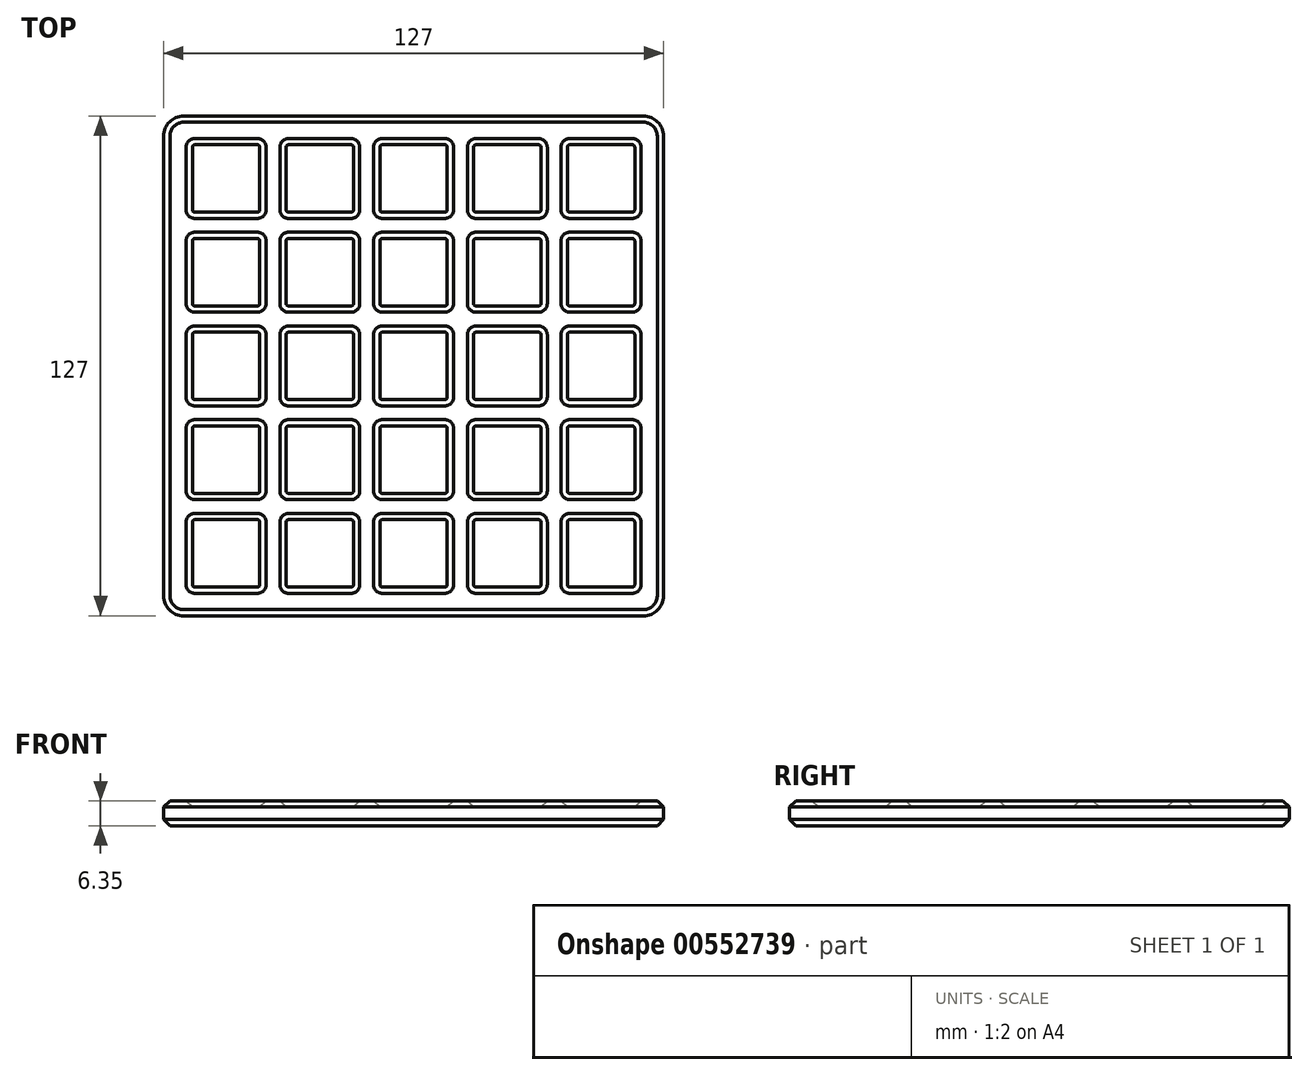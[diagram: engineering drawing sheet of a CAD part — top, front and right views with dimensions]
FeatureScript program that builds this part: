
annotation { "Feature Type Name" : "Feature", "Feature Type Description" : "" }
export const myFeature = defineFeature(function(context is Context, id is Id, definition is map)
    precondition{}
    {
        {
            var Q0;
            Q0=qCreatedBy(makeId("Top.planeOp"),FACE);
            var sketch = newSketch(context, id + "F0", { "sketchPlane" : qUnion([Q0])});
            skLineSegment(sketch, "E0.bottom", {"start": v(63.5, 63.5) * mm, "end": v(-63.5, 63.5) * mm});
            skLineSegment(sketch, "E0.top", {"start": v(63.5, -63.5) * mm, "end": v(-63.5, -63.5) * mm});
            skLineSegment(sketch, "E0.left", {"start": v(63.5, 63.5) * mm, "end": v(63.5, -63.5) * mm});
            skLineSegment(sketch, "E0.right", {"start": v(-63.5, 63.5) * mm, "end": v(-63.5, -63.5) * mm});
            skPoint(sketch, "E0.middle", {"position": v(0, 0) * mm});
            skLineSegment(sketch, "E1.bottom", {"start": v(8.57, 8.57) * mm, "end": v(-8.57, 8.57) * mm});
            skLineSegment(sketch, "E1.top", {"start": v(8.57, -8.57) * mm, "end": v(-8.57, -8.57) * mm});
            skLineSegment(sketch, "E1.left", {"start": v(8.57, 8.57) * mm, "end": v(8.57, -8.57) * mm});
            skLineSegment(sketch, "E1.right", {"start": v(-8.57, 8.57) * mm, "end": v(-8.57, -8.57) * mm});
            skLineSegment(sketch, "E2.1.0.0", {"start": v(32.39, 8.57) * mm, "end": v(15.24, 8.57) * mm});
            skLineSegment(sketch, "E2.1.0.1", {"start": v(15.24, 8.57) * mm, "end": v(15.24, -8.57) * mm});
            skLineSegment(sketch, "E2.1.0.2", {"start": v(32.39, -8.57) * mm, "end": v(15.24, -8.57) * mm});
            skLineSegment(sketch, "E2.1.0.3", {"start": v(32.39, 8.57) * mm, "end": v(32.39, -8.57) * mm});
            skLineSegment(sketch, "E2.2.0.0", {"start": v(56.2, 8.57) * mm, "end": v(39.05, 8.57) * mm});
            skLineSegment(sketch, "E2.2.0.1", {"start": v(39.05, 8.57) * mm, "end": v(39.05, -8.57) * mm});
            skLineSegment(sketch, "E2.2.0.2", {"start": v(56.2, -8.57) * mm, "end": v(39.05, -8.57) * mm});
            skLineSegment(sketch, "E2.2.0.3", {"start": v(56.2, 8.57) * mm, "end": v(56.2, -8.57) * mm});
            skLineSegment(sketch, "E2.direction1", {"start": v(-8.57, 8.57) * mm, "end": v(15.24, 8.57) * mm, "construction": true});
            skLineSegment(sketch, "E2.direction2", {"start": v(-8.57, 8.57) * mm, "end": v(-8.57, 32.39) * mm, "construction": true});
            skLineSegment(sketch, "E3.0.0.1", {"start": v(8.57, 32.39) * mm, "end": v(-8.57, 32.39) * mm});
            skLineSegment(sketch, "E3.3.0.1", {"start": v(-8.57, 32.39) * mm, "end": v(-8.57, 15.24) * mm});
            skLineSegment(sketch, "E3.6.0.1", {"start": v(8.57, 15.24) * mm, "end": v(-8.57, 15.24) * mm});
            skLineSegment(sketch, "E3.9.0.1", {"start": v(8.57, 32.39) * mm, "end": v(8.57, 15.24) * mm});
            skLineSegment(sketch, "E3.0.0.2", {"start": v(8.57, 56.2) * mm, "end": v(-8.57, 56.2) * mm});
            skLineSegment(sketch, "E3.3.0.2", {"start": v(-8.57, 56.2) * mm, "end": v(-8.57, 39.05) * mm});
            skLineSegment(sketch, "E3.6.0.2", {"start": v(8.57, 39.05) * mm, "end": v(-8.57, 39.05) * mm});
            skLineSegment(sketch, "E3.9.0.2", {"start": v(8.57, 56.2) * mm, "end": v(8.57, 39.05) * mm});
            skLineSegment(sketch, "E3.0.1.1", {"start": v(32.39, 32.39) * mm, "end": v(15.24, 32.39) * mm});
            skLineSegment(sketch, "E3.3.1.1", {"start": v(15.24, 32.39) * mm, "end": v(15.24, 15.24) * mm});
            skLineSegment(sketch, "E3.6.1.1", {"start": v(32.39, 15.24) * mm, "end": v(15.24, 15.24) * mm});
            skLineSegment(sketch, "E3.9.1.1", {"start": v(32.39, 32.39) * mm, "end": v(32.39, 15.24) * mm});
            skLineSegment(sketch, "E3.0.1.2", {"start": v(32.38, 56.2) * mm, "end": v(15.24, 56.2) * mm});
            skLineSegment(sketch, "E3.3.1.2", {"start": v(15.24, 56.2) * mm, "end": v(15.24, 39.05) * mm});
            skLineSegment(sketch, "E3.6.1.2", {"start": v(32.38, 39.05) * mm, "end": v(15.24, 39.05) * mm});
            skLineSegment(sketch, "E3.9.1.2", {"start": v(32.38, 56.2) * mm, "end": v(32.38, 39.05) * mm});
            skLineSegment(sketch, "E3.0.2.1", {"start": v(56.2, 32.39) * mm, "end": v(39.05, 32.39) * mm});
            skLineSegment(sketch, "E3.3.2.1", {"start": v(39.05, 32.39) * mm, "end": v(39.05, 15.24) * mm});
            skLineSegment(sketch, "E3.6.2.1", {"start": v(56.2, 15.24) * mm, "end": v(39.05, 15.24) * mm});
            skLineSegment(sketch, "E3.9.2.1", {"start": v(56.2, 32.39) * mm, "end": v(56.2, 15.24) * mm});
            skLineSegment(sketch, "E3.0.2.2", {"start": v(56.2, 56.2) * mm, "end": v(39.05, 56.2) * mm});
            skLineSegment(sketch, "E3.3.2.2", {"start": v(39.05, 56.2) * mm, "end": v(39.05, 39.05) * mm});
            skLineSegment(sketch, "E3.6.2.2", {"start": v(56.2, 39.05) * mm, "end": v(39.05, 39.05) * mm});
            skLineSegment(sketch, "E3.9.2.2", {"start": v(56.2, 56.2) * mm, "end": v(56.2, 39.05) * mm});
            skLineSegment(sketch, "E4.1.0.0", {"start": v(-32.39, 8.57) * mm, "end": v(-32.39, 32.39) * mm, "construction": true});
            skLineSegment(sketch, "E4.1.0.1", {"start": v(-32.39, 8.57) * mm, "end": v(-32.39, -8.57) * mm});
            skLineSegment(sketch, "E4.1.0.2", {"start": v(-15.24, 8.57) * mm, "end": v(-15.24, -8.57) * mm});
            skLineSegment(sketch, "E4.1.0.3", {"start": v(-15.24, 32.39) * mm, "end": v(-32.39, 32.39) * mm});
            skLineSegment(sketch, "E4.1.0.4", {"start": v(-15.24, 56.2) * mm, "end": v(-32.39, 56.2) * mm});
            skLineSegment(sketch, "E4.1.0.5", {"start": v(-15.24, 56.2) * mm, "end": v(-15.24, 39.05) * mm});
            skLineSegment(sketch, "E4.1.0.6", {"start": v(-15.24, -8.57) * mm, "end": v(-32.39, -8.57) * mm});
            skLineSegment(sketch, "E4.1.0.7", {"start": v(-15.24, 8.57) * mm, "end": v(-32.39, 8.57) * mm});
            skLineSegment(sketch, "E4.1.0.9", {"start": v(-32.39, 56.2) * mm, "end": v(-32.39, 39.05) * mm});
            skLineSegment(sketch, "E4.1.0.10", {"start": v(-15.24, 15.24) * mm, "end": v(-32.39, 15.24) * mm});
            skLineSegment(sketch, "E4.1.0.11", {"start": v(-15.24, 39.05) * mm, "end": v(-32.39, 39.05) * mm});
            skLineSegment(sketch, "E4.1.0.12", {"start": v(-15.24, 32.39) * mm, "end": v(-15.24, 15.24) * mm});
            skLineSegment(sketch, "E4.1.0.14", {"start": v(-32.39, 32.39) * mm, "end": v(-32.39, 15.24) * mm});
            skLineSegment(sketch, "E4.2.0.0", {"start": v(-56.2, 8.57) * mm, "end": v(-56.2, 32.38) * mm, "construction": true});
            skLineSegment(sketch, "E4.2.0.1", {"start": v(-56.2, 8.57) * mm, "end": v(-56.2, -8.57) * mm});
            skLineSegment(sketch, "E4.2.0.2", {"start": v(-39.05, 8.57) * mm, "end": v(-39.05, -8.57) * mm});
            skLineSegment(sketch, "E4.2.0.3", {"start": v(-39.05, 32.39) * mm, "end": v(-56.2, 32.39) * mm});
            skLineSegment(sketch, "E4.2.0.4", {"start": v(-39.05, 56.2) * mm, "end": v(-56.2, 56.2) * mm});
            skLineSegment(sketch, "E4.2.0.5", {"start": v(-39.05, 56.2) * mm, "end": v(-39.05, 39.05) * mm});
            skLineSegment(sketch, "E4.2.0.6", {"start": v(-39.05, -8.57) * mm, "end": v(-56.2, -8.57) * mm});
            skLineSegment(sketch, "E4.2.0.7", {"start": v(-39.05, 8.57) * mm, "end": v(-56.2, 8.57) * mm});
            skLineSegment(sketch, "E4.2.0.9", {"start": v(-56.2, 56.2) * mm, "end": v(-56.2, 39.05) * mm});
            skLineSegment(sketch, "E4.2.0.10", {"start": v(-39.05, 15.24) * mm, "end": v(-56.2, 15.24) * mm});
            skLineSegment(sketch, "E4.2.0.11", {"start": v(-39.05, 39.05) * mm, "end": v(-56.2, 39.05) * mm});
            skLineSegment(sketch, "E4.2.0.12", {"start": v(-39.05, 32.38) * mm, "end": v(-39.05, 15.24) * mm});
            skLineSegment(sketch, "E4.2.0.14", {"start": v(-56.2, 32.38) * mm, "end": v(-56.2, 15.24) * mm});
            skLineSegment(sketch, "E4.direction1", {"start": v(-8.57, -8.57) * mm, "end": v(-32.39, -8.57) * mm, "construction": true});
            skLineSegment(sketch, "E5.0.1.1", {"start": v(56.2, -32.38) * mm, "end": v(39.05, -32.38) * mm});
            skLineSegment(sketch, "E5.0.1.2", {"start": v(-15.24, -15.24) * mm, "end": v(-15.24, -32.38) * mm});
            skLineSegment(sketch, "E5.0.1.3", {"start": v(-8.57, -15.24) * mm, "end": v(-8.57, -32.39) * mm});
            skLineSegment(sketch, "E5.0.1.4", {"start": v(-15.24, -15.24) * mm, "end": v(-32.39, -15.24) * mm});
            skLineSegment(sketch, "E5.0.1.5", {"start": v(32.39, -15.24) * mm, "end": v(15.24, -15.24) * mm});
            skLineSegment(sketch, "E5.0.1.7", {"start": v(8.57, -15.24) * mm, "end": v(8.57, -32.38) * mm});
            skLineSegment(sketch, "E5.0.1.8", {"start": v(-39.05, -15.24) * mm, "end": v(-56.2, -15.24) * mm});
            skLineSegment(sketch, "E5.0.1.9", {"start": v(-39.05, -32.39) * mm, "end": v(-56.2, -32.39) * mm});
            skLineSegment(sketch, "E5.0.1.10", {"start": v(-8.57, -32.38) * mm, "end": v(-32.38, -32.39) * mm, "construction": true});
            skLineSegment(sketch, "E5.0.1.11", {"start": v(15.24, -15.24) * mm, "end": v(15.24, -32.39) * mm});
            skLineSegment(sketch, "E5.0.1.12", {"start": v(32.39, -32.38) * mm, "end": v(15.24, -32.38) * mm});
            skLineSegment(sketch, "E5.0.1.13", {"start": v(32.39, -15.24) * mm, "end": v(32.39, -32.38) * mm});
            skLineSegment(sketch, "E5.0.1.14", {"start": v(56.2, -15.24) * mm, "end": v(39.05, -15.24) * mm});
            skLineSegment(sketch, "E5.0.1.15", {"start": v(-39.05, -15.24) * mm, "end": v(-39.05, -32.39) * mm});
            skLineSegment(sketch, "E5.0.1.16", {"start": v(-32.39, -15.24) * mm, "end": v(-32.39, -32.39) * mm});
            skLineSegment(sketch, "E5.0.1.17", {"start": v(39.05, -15.24) * mm, "end": v(39.05, -32.39) * mm});
            skLineSegment(sketch, "E5.0.1.18", {"start": v(-8.57, -15.24) * mm, "end": v(15.24, -15.24) * mm, "construction": true});
            skLineSegment(sketch, "E5.0.1.19", {"start": v(-56.2, -15.24) * mm, "end": v(-56.2, -32.39) * mm});
            skLineSegment(sketch, "E5.0.1.20", {"start": v(8.57, -32.38) * mm, "end": v(-8.57, -32.38) * mm});
            skLineSegment(sketch, "E5.0.1.21", {"start": v(56.2, -15.24) * mm, "end": v(56.2, -32.38) * mm});
            skLineSegment(sketch, "E5.0.1.22", {"start": v(-15.24, -32.39) * mm, "end": v(-32.38, -32.39) * mm});
            skLineSegment(sketch, "E5.0.1.25", {"start": v(8.57, -15.24) * mm, "end": v(-8.57, -15.24) * mm});
            skLineSegment(sketch, "E5.0.2.1", {"start": v(56.2, -56.2) * mm, "end": v(39.05, -56.2) * mm});
            skLineSegment(sketch, "E5.0.2.2", {"start": v(-15.24, -39.05) * mm, "end": v(-15.24, -56.2) * mm});
            skLineSegment(sketch, "E5.0.2.3", {"start": v(-8.57, -39.05) * mm, "end": v(-8.57, -56.2) * mm});
            skLineSegment(sketch, "E5.0.2.4", {"start": v(-15.24, -39.05) * mm, "end": v(-32.38, -39.05) * mm});
            skLineSegment(sketch, "E5.0.2.5", {"start": v(32.39, -39.05) * mm, "end": v(15.24, -39.05) * mm});
            skLineSegment(sketch, "E5.0.2.7", {"start": v(8.57, -39.05) * mm, "end": v(8.57, -56.2) * mm});
            skLineSegment(sketch, "E5.0.2.8", {"start": v(-39.05, -39.05) * mm, "end": v(-56.2, -39.05) * mm});
            skLineSegment(sketch, "E5.0.2.9", {"start": v(-39.05, -56.2) * mm, "end": v(-56.2, -56.2) * mm});
            skLineSegment(sketch, "E5.0.2.10", {"start": v(-8.57, -56.2) * mm, "end": v(-32.38, -56.2) * mm, "construction": true});
            skLineSegment(sketch, "E5.0.2.11", {"start": v(15.24, -39.05) * mm, "end": v(15.24, -56.2) * mm});
            skLineSegment(sketch, "E5.0.2.12", {"start": v(32.39, -56.2) * mm, "end": v(15.24, -56.2) * mm});
            skLineSegment(sketch, "E5.0.2.13", {"start": v(32.39, -39.05) * mm, "end": v(32.39, -56.2) * mm});
            skLineSegment(sketch, "E5.0.2.14", {"start": v(56.2, -39.05) * mm, "end": v(39.05, -39.05) * mm});
            skLineSegment(sketch, "E5.0.2.15", {"start": v(-39.05, -39.05) * mm, "end": v(-39.05, -56.2) * mm});
            skLineSegment(sketch, "E5.0.2.16", {"start": v(-32.38, -39.05) * mm, "end": v(-32.38, -56.2) * mm});
            skLineSegment(sketch, "E5.0.2.17", {"start": v(39.05, -39.05) * mm, "end": v(39.05, -56.2) * mm});
            skLineSegment(sketch, "E5.0.2.18", {"start": v(-8.57, -39.05) * mm, "end": v(15.24, -39.05) * mm, "construction": true});
            skLineSegment(sketch, "E5.0.2.19", {"start": v(-56.2, -39.05) * mm, "end": v(-56.2, -56.2) * mm});
            skLineSegment(sketch, "E5.0.2.20", {"start": v(8.57, -56.2) * mm, "end": v(-8.57, -56.2) * mm});
            skLineSegment(sketch, "E5.0.2.21", {"start": v(56.2, -39.05) * mm, "end": v(56.2, -56.2) * mm});
            skLineSegment(sketch, "E5.0.2.22", {"start": v(-15.24, -56.2) * mm, "end": v(-32.38, -56.2) * mm});
            skLineSegment(sketch, "E5.0.2.25", {"start": v(8.57, -39.05) * mm, "end": v(-8.57, -39.05) * mm});
            skLineSegment(sketch, "E5.direction1", {"start": v(-56.2, -8.57) * mm, "end": v(-30.8, -8.57) * mm, "construction": true});
            skLineSegment(sketch, "E5.direction2", {"start": v(-56.2, -8.57) * mm, "end": v(-56.2, -32.39) * mm, "construction": true});
            skSolve(sketch);
        }
        {
            var Q0;
            Q0=makeQuery(id+"F0.imprint","IMPRINT",FACE,{"disambiguationData":[TD([[makeQuery(id+"F0.imprint","IMPRINT",EDGE,{"derivedFrom":sQuery(id+"F0.wireOp",EDGE,"E0.bottom")}),1.0]])]});
            extrude(context, id + "F1", {"entities" : qUnion([Q0]), "depth" : 6.35 * mm, "offsetDistance" : 25.4 * mm});
        }
        {
            var Q0;
            Q0=makeQuery(id+"F0.imprint","IMPRINT",FACE,{"disambiguationData":[TD([[makeQuery(id+"F0.imprint","IMPRINT",EDGE,{"derivedFrom":sQuery(id+"F0.wireOp",EDGE,"E5.0.2.8")}),1.0]])]});
            var Q1;
            Q1=makeQuery(id+"F0.imprint","IMPRINT",FACE,{"disambiguationData":[TD([[makeQuery(id+"F0.imprint","IMPRINT",EDGE,{"derivedFrom":sQuery(id+"F0.wireOp",EDGE,"E5.0.1.8")}),1.0]])]});
            var Q2;
            Q2=makeQuery(id+"F0.imprint","IMPRINT",FACE,{"disambiguationData":[TD([[makeQuery(id+"F0.imprint","IMPRINT",EDGE,{"derivedFrom":sQuery(id+"F0.wireOp",EDGE,"E4.2.0.1")}),1.0]])]});
            var Q3;
            Q3=makeQuery(id+"F0.imprint","IMPRINT",FACE,{"disambiguationData":[TD([[makeQuery(id+"F0.imprint","IMPRINT",EDGE,{"derivedFrom":sQuery(id+"F0.wireOp",EDGE,"E4.2.0.3")}),1.0]])]});
            var Q4;
            Q4=makeQuery(id+"F0.imprint","IMPRINT",FACE,{"disambiguationData":[TD([[makeQuery(id+"F0.imprint","IMPRINT",EDGE,{"derivedFrom":sQuery(id+"F0.wireOp",EDGE,"E4.2.0.4")}),1.0]])]});
            var Q5;
            Q5=makeQuery(id+"F0.imprint","IMPRINT",FACE,{"disambiguationData":[TD([[makeQuery(id+"F0.imprint","IMPRINT",EDGE,{"derivedFrom":sQuery(id+"F0.wireOp",EDGE,"E4.1.0.4")}),1.0]])]});
            var Q6;
            Q6=makeQuery(id+"F0.imprint","IMPRINT",FACE,{"disambiguationData":[TD([[makeQuery(id+"F0.imprint","IMPRINT",EDGE,{"derivedFrom":sQuery(id+"F0.wireOp",EDGE,"E4.1.0.3")}),1.0]])]});
            var Q7;
            Q7=makeQuery(id+"F0.imprint","IMPRINT",FACE,{"disambiguationData":[TD([[makeQuery(id+"F0.imprint","IMPRINT",EDGE,{"derivedFrom":sQuery(id+"F0.wireOp",EDGE,"E4.1.0.1")}),1.0]])]});
            var Q8;
            Q8=makeQuery(id+"F0.imprint","IMPRINT",FACE,{"disambiguationData":[TD([[makeQuery(id+"F0.imprint","IMPRINT",EDGE,{"derivedFrom":sQuery(id+"F0.wireOp",EDGE,"E5.0.1.2")}),-1.0]])]});
            var Q9;
            Q9=makeQuery(id+"F0.imprint","IMPRINT",FACE,{"disambiguationData":[TD([[makeQuery(id+"F0.imprint","IMPRINT",EDGE,{"derivedFrom":sQuery(id+"F0.wireOp",EDGE,"E5.0.2.2")}),-1.0]])]});
            var Q10;
            Q10=makeQuery(id+"F0.imprint","IMPRINT",FACE,{"disambiguationData":[TD([[makeQuery(id+"F0.imprint","IMPRINT",EDGE,{"derivedFrom":sQuery(id+"F0.wireOp",EDGE,"E5.0.2.3")}),1.0]])]});
            var Q11;
            Q11=makeQuery(id+"F0.imprint","IMPRINT",FACE,{"disambiguationData":[TD([[makeQuery(id+"F0.imprint","IMPRINT",EDGE,{"derivedFrom":sQuery(id+"F0.wireOp",EDGE,"E5.0.1.3")}),1.0]])]});
            var Q12;
            Q12=makeQuery(id+"F0.imprint","IMPRINT",FACE,{"disambiguationData":[TD([[makeQuery(id+"F0.imprint","IMPRINT",EDGE,{"derivedFrom":sQuery(id+"F0.wireOp",EDGE,"E1.bottom")}),1.0]])]});
            var Q13;
            Q13=makeQuery(id+"F0.imprint","IMPRINT",FACE,{"disambiguationData":[TD([[makeQuery(id+"F0.imprint","IMPRINT",EDGE,{"derivedFrom":sQuery(id+"F0.wireOp",EDGE,"E3.0.0.1")}),1.0]])]});
            var Q14;
            Q14=makeQuery(id+"F0.imprint","IMPRINT",FACE,{"disambiguationData":[TD([[makeQuery(id+"F0.imprint","IMPRINT",EDGE,{"derivedFrom":sQuery(id+"F0.wireOp",EDGE,"E3.0.0.2")}),1.0]])]});
            var Q15;
            Q15=makeQuery(id+"F0.imprint","IMPRINT",FACE,{"disambiguationData":[TD([[makeQuery(id+"F0.imprint","IMPRINT",EDGE,{"derivedFrom":sQuery(id+"F0.wireOp",EDGE,"E3.0.1.2")}),1.0]])]});
            var Q16;
            Q16=makeQuery(id+"F0.imprint","IMPRINT",FACE,{"disambiguationData":[TD([[makeQuery(id+"F0.imprint","IMPRINT",EDGE,{"derivedFrom":sQuery(id+"F0.wireOp",EDGE,"E3.0.1.1")}),1.0]])]});
            var Q17;
            Q17=makeQuery(id+"F0.imprint","IMPRINT",FACE,{"disambiguationData":[TD([[makeQuery(id+"F0.imprint","IMPRINT",EDGE,{"derivedFrom":sQuery(id+"F0.wireOp",EDGE,"E2.1.0.0")}),1.0]])]});
            var Q18;
            Q18=makeQuery(id+"F0.imprint","IMPRINT",FACE,{"disambiguationData":[TD([[makeQuery(id+"F0.imprint","IMPRINT",EDGE,{"derivedFrom":sQuery(id+"F0.wireOp",EDGE,"E5.0.1.5")}),1.0]])]});
            var Q19;
            Q19=makeQuery(id+"F0.imprint","IMPRINT",FACE,{"disambiguationData":[TD([[makeQuery(id+"F0.imprint","IMPRINT",EDGE,{"derivedFrom":sQuery(id+"F0.wireOp",EDGE,"E5.0.2.5")}),1.0]])]});
            var Q20;
            Q20=makeQuery(id+"F0.imprint","IMPRINT",FACE,{"disambiguationData":[TD([[makeQuery(id+"F0.imprint","IMPRINT",EDGE,{"derivedFrom":sQuery(id+"F0.wireOp",EDGE,"E5.0.2.1")}),-1.0]])]});
            var Q21;
            Q21=makeQuery(id+"F0.imprint","IMPRINT",FACE,{"disambiguationData":[TD([[makeQuery(id+"F0.imprint","IMPRINT",EDGE,{"derivedFrom":sQuery(id+"F0.wireOp",EDGE,"E5.0.1.1")}),-1.0]])]});
            var Q22;
            Q22=makeQuery(id+"F0.imprint","IMPRINT",FACE,{"disambiguationData":[TD([[makeQuery(id+"F0.imprint","IMPRINT",EDGE,{"derivedFrom":sQuery(id+"F0.wireOp",EDGE,"E2.2.0.0")}),1.0]])]});
            var Q23;
            Q23=makeQuery(id+"F0.imprint","IMPRINT",FACE,{"disambiguationData":[TD([[makeQuery(id+"F0.imprint","IMPRINT",EDGE,{"derivedFrom":sQuery(id+"F0.wireOp",EDGE,"E3.0.2.2")}),1.0]])]});
            var Q24;
            Q24=makeQuery(id+"F0.imprint","IMPRINT",FACE,{"disambiguationData":[TD([[makeQuery(id+"F0.imprint","IMPRINT",EDGE,{"derivedFrom":sQuery(id+"F0.wireOp",EDGE,"E3.0.2.1")}),1.0]])]});
            extrude(context, id + "F2", {"entities" : qUnion([Q0, Q1, Q2, Q3, Q4, Q5, Q6, Q7, Q8, Q9, Q10, Q11, Q12, Q13, Q14, Q15, Q16, Q17, Q18, Q19, Q20, Q21, Q22, Q23, Q24]), "operationType" : NewBodyOperationType.ADD, "flatOperationType" : FlatOperationType.REMOVE, "depth" : 4.76 * mm, "offsetDistance" : 25.4 * mm, "domain" : OperationDomain.MODEL});
        }
        {
            var Q0;
            Q0=makeQuery(id+"F1.opExtrude","SWEPT_EDGE",EDGE,{"disambiguationData":[OSD([sQuery(id+"F0.wireOp",EDGE,"E5.0.2.8"),sQuery(id+"F0.wireOp",EDGE,"E5.0.2.19")])]});
            var Q1;
            Q1=makeQuery(id+"F1.opExtrude","SWEPT_EDGE",EDGE,{"disambiguationData":[OSD([sQuery(id+"F0.wireOp",EDGE,"E5.0.1.4"),sQuery(id+"F0.wireOp",EDGE,"E5.0.1.16")])]});
            var Q2;
            Q2=makeQuery(id+"F1.opExtrude","SWEPT_EDGE",EDGE,{"disambiguationData":[OSD([sQuery(id+"F0.wireOp",EDGE,"E4.1.0.1"),sQuery(id+"F0.wireOp",EDGE,"E4.1.0.7")])]});
            var Q3;
            Q3=makeQuery(id+"F1.opExtrude","SWEPT_EDGE",EDGE,{"disambiguationData":[OSD([sQuery(id+"F0.wireOp",EDGE,"E4.1.0.3"),sQuery(id+"F0.wireOp",EDGE,"E4.1.0.14")])]});
            var Q4;
            Q4=makeQuery(id+"F1.opExtrude","SWEPT_EDGE",EDGE,{"disambiguationData":[OSD([sQuery(id+"F0.wireOp",EDGE,"E4.2.0.1"),sQuery(id+"F0.wireOp",EDGE,"E4.2.0.7")])]});
            var Q5;
            Q5=makeQuery(id+"F1.opExtrude","SWEPT_EDGE",EDGE,{"disambiguationData":[OSD([sQuery(id+"F0.wireOp",EDGE,"E1.bottom"),sQuery(id+"F0.wireOp",EDGE,"E1.right")])]});
            var Q6;
            Q6=makeQuery(id+"F1.opExtrude","SWEPT_EDGE",EDGE,{"disambiguationData":[OSD([sQuery(id+"F0.wireOp",EDGE,"E5.0.1.3"),sQuery(id+"F0.wireOp",EDGE,"E5.0.1.25")])]});
            var Q7;
            Q7=makeQuery(id+"F1.opExtrude","SWEPT_EDGE",EDGE,{"disambiguationData":[OSD([sQuery(id+"F0.wireOp",EDGE,"E5.0.2.3"),sQuery(id+"F0.wireOp",EDGE,"E5.0.2.25")])]});
            var Q8;
            Q8=makeQuery(id+"F1.opExtrude","SWEPT_EDGE",EDGE,{"disambiguationData":[OSD([sQuery(id+"F0.wireOp",EDGE,"E5.0.2.4"),sQuery(id+"F0.wireOp",EDGE,"E5.0.2.16")])]});
            var Q9;
            Q9=makeQuery(id+"F1.opExtrude","SWEPT_EDGE",EDGE,{"disambiguationData":[OSD([sQuery(id+"F0.wireOp",EDGE,"E3.0.0.1"),sQuery(id+"F0.wireOp",EDGE,"E3.3.0.1")])]});
            var Q10;
            Q10=makeQuery(id+"F1.opExtrude","SWEPT_EDGE",EDGE,{"disambiguationData":[OSD([sQuery(id+"F0.wireOp",EDGE,"E3.0.0.2"),sQuery(id+"F0.wireOp",EDGE,"E3.3.0.2")])]});
            var Q11;
            Q11=makeQuery(id+"F1.opExtrude","SWEPT_EDGE",EDGE,{"disambiguationData":[OSD([sQuery(id+"F0.wireOp",EDGE,"E4.1.0.4"),sQuery(id+"F0.wireOp",EDGE,"E4.1.0.9")])]});
            var Q12;
            Q12=makeQuery(id+"F1.opExtrude","SWEPT_EDGE",EDGE,{"disambiguationData":[OSD([sQuery(id+"F0.wireOp",EDGE,"E5.0.1.8"),sQuery(id+"F0.wireOp",EDGE,"E5.0.1.19")])]});
            var Q13;
            Q13=makeQuery(id+"F1.opExtrude","SWEPT_EDGE",EDGE,{"disambiguationData":[OSD([sQuery(id+"F0.wireOp",EDGE,"E4.2.0.3"),sQuery(id+"F0.wireOp",EDGE,"E4.2.0.14")])]});
            var Q14;
            Q14=makeQuery(id+"F1.opExtrude","SWEPT_EDGE",EDGE,{"disambiguationData":[OSD([sQuery(id+"F0.wireOp",EDGE,"E4.2.0.4"),sQuery(id+"F0.wireOp",EDGE,"E4.2.0.9")])]});
            var Q15;
            Q15=makeQuery(id+"F1.opExtrude","SWEPT_EDGE",EDGE,{"disambiguationData":[OSD([sQuery(id+"F0.wireOp",EDGE,"E3.0.1.2"),sQuery(id+"F0.wireOp",EDGE,"E3.3.1.2")])]});
            var Q16;
            Q16=makeQuery(id+"F1.opExtrude","SWEPT_EDGE",EDGE,{"disambiguationData":[OSD([sQuery(id+"F0.wireOp",EDGE,"E3.0.2.2"),sQuery(id+"F0.wireOp",EDGE,"E3.3.2.2")])]});
            var Q17;
            Q17=makeQuery(id+"F1.opExtrude","SWEPT_EDGE",EDGE,{"disambiguationData":[OSD([sQuery(id+"F0.wireOp",EDGE,"E3.0.2.1"),sQuery(id+"F0.wireOp",EDGE,"E3.3.2.1")])]});
            var Q18;
            Q18=makeQuery(id+"F1.opExtrude","SWEPT_EDGE",EDGE,{"disambiguationData":[OSD([sQuery(id+"F0.wireOp",EDGE,"E3.0.1.1"),sQuery(id+"F0.wireOp",EDGE,"E3.3.1.1")])]});
            var Q19;
            Q19=makeQuery(id+"F1.opExtrude","SWEPT_EDGE",EDGE,{"disambiguationData":[OSD([sQuery(id+"F0.wireOp",EDGE,"E2.1.0.0"),sQuery(id+"F0.wireOp",EDGE,"E2.1.0.1")])]});
            var Q20;
            Q20=makeQuery(id+"F1.opExtrude","SWEPT_EDGE",EDGE,{"disambiguationData":[OSD([sQuery(id+"F0.wireOp",EDGE,"E2.2.0.0"),sQuery(id+"F0.wireOp",EDGE,"E2.2.0.1")])]});
            var Q21;
            Q21=makeQuery(id+"F1.opExtrude","SWEPT_EDGE",EDGE,{"disambiguationData":[OSD([sQuery(id+"F0.wireOp",EDGE,"E5.0.1.14"),sQuery(id+"F0.wireOp",EDGE,"E5.0.1.17")])]});
            var Q22;
            Q22=makeQuery(id+"F1.opExtrude","SWEPT_EDGE",EDGE,{"disambiguationData":[OSD([sQuery(id+"F0.wireOp",EDGE,"E5.0.1.5"),sQuery(id+"F0.wireOp",EDGE,"E5.0.1.11")])]});
            var Q23;
            Q23=makeQuery(id+"F1.opExtrude","SWEPT_EDGE",EDGE,{"disambiguationData":[OSD([sQuery(id+"F0.wireOp",EDGE,"E5.0.2.5"),sQuery(id+"F0.wireOp",EDGE,"E5.0.2.11")])]});
            var Q24;
            Q24=makeQuery(id+"F1.opExtrude","SWEPT_EDGE",EDGE,{"disambiguationData":[OSD([sQuery(id+"F0.wireOp",EDGE,"E5.0.2.14"),sQuery(id+"F0.wireOp",EDGE,"E5.0.2.17")])]});
            var Q25;
            Q25=makeQuery(id+"F1.opExtrude","SWEPT_EDGE",EDGE,{"disambiguationData":[OSD([sQuery(id+"F0.wireOp",EDGE,"E5.0.2.1"),sQuery(id+"F0.wireOp",EDGE,"E5.0.2.21")])]});
            var Q26;
            Q26=makeQuery(id+"F1.opExtrude","SWEPT_EDGE",EDGE,{"disambiguationData":[OSD([sQuery(id+"F0.wireOp",EDGE,"E5.0.1.1"),sQuery(id+"F0.wireOp",EDGE,"E5.0.1.21")])]});
            var Q27;
            Q27=makeQuery(id+"F1.opExtrude","SWEPT_EDGE",EDGE,{"disambiguationData":[OSD([sQuery(id+"F0.wireOp",EDGE,"E5.0.1.12"),sQuery(id+"F0.wireOp",EDGE,"E5.0.1.13")])]});
            var Q28;
            Q28=makeQuery(id+"F1.opExtrude","SWEPT_EDGE",EDGE,{"disambiguationData":[OSD([sQuery(id+"F0.wireOp",EDGE,"E5.0.2.12"),sQuery(id+"F0.wireOp",EDGE,"E5.0.2.13")])]});
            var Q29;
            Q29=makeQuery(id+"F1.opExtrude","SWEPT_EDGE",EDGE,{"disambiguationData":[OSD([sQuery(id+"F0.wireOp",EDGE,"E5.0.1.2"),sQuery(id+"F0.wireOp",EDGE,"E5.0.1.22")])]});
            var Q30;
            Q30=makeQuery(id+"F1.opExtrude","SWEPT_EDGE",EDGE,{"disambiguationData":[OSD([sQuery(id+"F0.wireOp",EDGE,"E5.0.1.7"),sQuery(id+"F0.wireOp",EDGE,"E5.0.1.20")])]});
            var Q31;
            Q31=makeQuery(id+"F1.opExtrude","SWEPT_EDGE",EDGE,{"disambiguationData":[OSD([sQuery(id+"F0.wireOp",EDGE,"E5.0.2.7"),sQuery(id+"F0.wireOp",EDGE,"E5.0.2.20")])]});
            var Q32;
            Q32=makeQuery(id+"F1.opExtrude","SWEPT_EDGE",EDGE,{"disambiguationData":[OSD([sQuery(id+"F0.wireOp",EDGE,"E5.0.2.2"),sQuery(id+"F0.wireOp",EDGE,"E5.0.2.22")])]});
            var Q33;
            Q33=makeQuery(id+"F1.opExtrude","SWEPT_EDGE",EDGE,{"disambiguationData":[OSD([sQuery(id+"F0.wireOp",EDGE,"E5.0.2.9"),sQuery(id+"F0.wireOp",EDGE,"E5.0.2.15")])]});
            var Q34;
            Q34=makeQuery(id+"F1.opExtrude","SWEPT_EDGE",EDGE,{"disambiguationData":[OSD([sQuery(id+"F0.wireOp",EDGE,"E3.6.0.2"),sQuery(id+"F0.wireOp",EDGE,"E3.9.0.2")])]});
            var Q35;
            Q35=makeQuery(id+"F1.opExtrude","SWEPT_EDGE",EDGE,{"disambiguationData":[OSD([sQuery(id+"F0.wireOp",EDGE,"E3.6.0.1"),sQuery(id+"F0.wireOp",EDGE,"E3.9.0.1")])]});
            var Q36;
            Q36=makeQuery(id+"F1.opExtrude","SWEPT_EDGE",EDGE,{"disambiguationData":[OSD([sQuery(id+"F0.wireOp",EDGE,"E1.top"),sQuery(id+"F0.wireOp",EDGE,"E1.left")])]});
            var Q37;
            Q37=makeQuery(id+"F1.opExtrude","SWEPT_EDGE",EDGE,{"disambiguationData":[OSD([sQuery(id+"F0.wireOp",EDGE,"E2.1.0.2"),sQuery(id+"F0.wireOp",EDGE,"E2.1.0.3")])]});
            var Q38;
            Q38=makeQuery(id+"F1.opExtrude","SWEPT_EDGE",EDGE,{"disambiguationData":[OSD([sQuery(id+"F0.wireOp",EDGE,"E2.2.0.2"),sQuery(id+"F0.wireOp",EDGE,"E2.2.0.3")])]});
            var Q39;
            Q39=makeQuery(id+"F1.opExtrude","SWEPT_EDGE",EDGE,{"disambiguationData":[OSD([sQuery(id+"F0.wireOp",EDGE,"E3.6.2.1"),sQuery(id+"F0.wireOp",EDGE,"E3.9.2.1")])]});
            var Q40;
            Q40=makeQuery(id+"F1.opExtrude","SWEPT_EDGE",EDGE,{"disambiguationData":[OSD([sQuery(id+"F0.wireOp",EDGE,"E3.6.2.2"),sQuery(id+"F0.wireOp",EDGE,"E3.9.2.2")])]});
            var Q41;
            Q41=makeQuery(id+"F1.opExtrude","SWEPT_EDGE",EDGE,{"disambiguationData":[OSD([sQuery(id+"F0.wireOp",EDGE,"E3.6.1.2"),sQuery(id+"F0.wireOp",EDGE,"E3.9.1.2")])]});
            var Q42;
            Q42=makeQuery(id+"F1.opExtrude","SWEPT_EDGE",EDGE,{"disambiguationData":[OSD([sQuery(id+"F0.wireOp",EDGE,"E3.6.1.1"),sQuery(id+"F0.wireOp",EDGE,"E3.9.1.1")])]});
            var Q43;
            Q43=makeQuery(id+"F1.opExtrude","SWEPT_EDGE",EDGE,{"disambiguationData":[OSD([sQuery(id+"F0.wireOp",EDGE,"E4.1.0.5"),sQuery(id+"F0.wireOp",EDGE,"E4.1.0.11")])]});
            var Q44;
            Q44=makeQuery(id+"F1.opExtrude","SWEPT_EDGE",EDGE,{"disambiguationData":[OSD([sQuery(id+"F0.wireOp",EDGE,"E4.1.0.10"),sQuery(id+"F0.wireOp",EDGE,"E4.1.0.12")])]});
            var Q45;
            Q45=makeQuery(id+"F1.opExtrude","SWEPT_EDGE",EDGE,{"disambiguationData":[OSD([sQuery(id+"F0.wireOp",EDGE,"E4.1.0.2"),sQuery(id+"F0.wireOp",EDGE,"E4.1.0.6")])]});
            var Q46;
            Q46=makeQuery(id+"F1.opExtrude","SWEPT_EDGE",EDGE,{"disambiguationData":[OSD([sQuery(id+"F0.wireOp",EDGE,"E5.0.1.9"),sQuery(id+"F0.wireOp",EDGE,"E5.0.1.15")])]});
            var Q47;
            Q47=makeQuery(id+"F1.opExtrude","SWEPT_EDGE",EDGE,{"disambiguationData":[OSD([sQuery(id+"F0.wireOp",EDGE,"E4.2.0.2"),sQuery(id+"F0.wireOp",EDGE,"E4.2.0.6")])]});
            var Q48;
            Q48=makeQuery(id+"F1.opExtrude","SWEPT_EDGE",EDGE,{"disambiguationData":[OSD([sQuery(id+"F0.wireOp",EDGE,"E4.2.0.10"),sQuery(id+"F0.wireOp",EDGE,"E4.2.0.12")])]});
            var Q49;
            Q49=makeQuery(id+"F1.opExtrude","SWEPT_EDGE",EDGE,{"disambiguationData":[OSD([sQuery(id+"F0.wireOp",EDGE,"E4.2.0.5"),sQuery(id+"F0.wireOp",EDGE,"E4.2.0.11")])]});
            var Q50;
            Q50=makeQuery(id+"F1.opExtrude","SWEPT_EDGE",EDGE,{"disambiguationData":[OSD([sQuery(id+"F0.wireOp",EDGE,"E4.2.0.10"),sQuery(id+"F0.wireOp",EDGE,"E4.2.0.14")])]});
            var Q51;
            Q51=makeQuery(id+"F1.opExtrude","SWEPT_EDGE",EDGE,{"disambiguationData":[OSD([sQuery(id+"F0.wireOp",EDGE,"E4.2.0.9"),sQuery(id+"F0.wireOp",EDGE,"E4.2.0.11")])]});
            var Q52;
            Q52=makeQuery(id+"F1.opExtrude","SWEPT_EDGE",EDGE,{"disambiguationData":[OSD([sQuery(id+"F0.wireOp",EDGE,"E4.2.0.1"),sQuery(id+"F0.wireOp",EDGE,"E4.2.0.6")])]});
            var Q53;
            Q53=makeQuery(id+"F1.opExtrude","SWEPT_EDGE",EDGE,{"disambiguationData":[OSD([sQuery(id+"F0.wireOp",EDGE,"E5.0.1.9"),sQuery(id+"F0.wireOp",EDGE,"E5.0.1.19")])]});
            var Q54;
            Q54=makeQuery(id+"F1.opExtrude","SWEPT_EDGE",EDGE,{"disambiguationData":[OSD([sQuery(id+"F0.wireOp",EDGE,"E5.0.2.9"),sQuery(id+"F0.wireOp",EDGE,"E5.0.2.19")])]});
            var Q55;
            Q55=makeQuery(id+"F1.opExtrude","SWEPT_EDGE",EDGE,{"disambiguationData":[OSD([sQuery(id+"F0.wireOp",EDGE,"E5.0.2.16"),sQuery(id+"F0.wireOp",EDGE,"E5.0.2.22")])]});
            var Q56;
            Q56=makeQuery(id+"F1.opExtrude","SWEPT_EDGE",EDGE,{"disambiguationData":[OSD([sQuery(id+"F0.wireOp",EDGE,"E5.0.1.16"),sQuery(id+"F0.wireOp",EDGE,"E5.0.1.22")])]});
            var Q57;
            Q57=makeQuery(id+"F1.opExtrude","SWEPT_EDGE",EDGE,{"disambiguationData":[OSD([sQuery(id+"F0.wireOp",EDGE,"E4.1.0.1"),sQuery(id+"F0.wireOp",EDGE,"E4.1.0.6")])]});
            var Q58;
            Q58=makeQuery(id+"F1.opExtrude","SWEPT_EDGE",EDGE,{"disambiguationData":[OSD([sQuery(id+"F0.wireOp",EDGE,"E4.1.0.10"),sQuery(id+"F0.wireOp",EDGE,"E4.1.0.14")])]});
            var Q59;
            Q59=makeQuery(id+"F1.opExtrude","SWEPT_EDGE",EDGE,{"disambiguationData":[OSD([sQuery(id+"F0.wireOp",EDGE,"E4.1.0.9"),sQuery(id+"F0.wireOp",EDGE,"E4.1.0.11")])]});
            var Q60;
            Q60=makeQuery(id+"F1.opExtrude","SWEPT_EDGE",EDGE,{"disambiguationData":[OSD([sQuery(id+"F0.wireOp",EDGE,"E5.0.2.3"),sQuery(id+"F0.wireOp",EDGE,"E5.0.2.20")])]});
            var Q61;
            Q61=makeQuery(id+"F1.opExtrude","SWEPT_EDGE",EDGE,{"disambiguationData":[OSD([sQuery(id+"F0.wireOp",EDGE,"E5.0.1.3"),sQuery(id+"F0.wireOp",EDGE,"E5.0.1.20")])]});
            var Q62;
            Q62=makeQuery(id+"F1.opExtrude","SWEPT_EDGE",EDGE,{"disambiguationData":[OSD([sQuery(id+"F0.wireOp",EDGE,"E1.top"),sQuery(id+"F0.wireOp",EDGE,"E1.right")])]});
            var Q63;
            Q63=makeQuery(id+"F1.opExtrude","SWEPT_EDGE",EDGE,{"disambiguationData":[OSD([sQuery(id+"F0.wireOp",EDGE,"E3.3.0.1"),sQuery(id+"F0.wireOp",EDGE,"E3.6.0.1")])]});
            var Q64;
            Q64=makeQuery(id+"F1.opExtrude","SWEPT_EDGE",EDGE,{"disambiguationData":[OSD([sQuery(id+"F0.wireOp",EDGE,"E3.3.0.2"),sQuery(id+"F0.wireOp",EDGE,"E3.6.0.2")])]});
            var Q65;
            Q65=makeQuery(id+"F1.opExtrude","SWEPT_EDGE",EDGE,{"disambiguationData":[OSD([sQuery(id+"F0.wireOp",EDGE,"E3.3.1.2"),sQuery(id+"F0.wireOp",EDGE,"E3.6.1.2")])]});
            var Q66;
            Q66=makeQuery(id+"F1.opExtrude","SWEPT_EDGE",EDGE,{"disambiguationData":[OSD([sQuery(id+"F0.wireOp",EDGE,"E3.3.1.1"),sQuery(id+"F0.wireOp",EDGE,"E3.6.1.1")])]});
            var Q67;
            Q67=makeQuery(id+"F1.opExtrude","SWEPT_EDGE",EDGE,{"disambiguationData":[OSD([sQuery(id+"F0.wireOp",EDGE,"E2.1.0.1"),sQuery(id+"F0.wireOp",EDGE,"E2.1.0.2")])]});
            var Q68;
            Q68=makeQuery(id+"F1.opExtrude","SWEPT_EDGE",EDGE,{"disambiguationData":[OSD([sQuery(id+"F0.wireOp",EDGE,"E5.0.1.11"),sQuery(id+"F0.wireOp",EDGE,"E5.0.1.12")])]});
            var Q69;
            Q69=makeQuery(id+"F1.opExtrude","SWEPT_EDGE",EDGE,{"disambiguationData":[OSD([sQuery(id+"F0.wireOp",EDGE,"E5.0.2.11"),sQuery(id+"F0.wireOp",EDGE,"E5.0.2.12")])]});
            var Q70;
            Q70=makeQuery(id+"F1.opExtrude","SWEPT_EDGE",EDGE,{"disambiguationData":[OSD([sQuery(id+"F0.wireOp",EDGE,"E5.0.2.1"),sQuery(id+"F0.wireOp",EDGE,"E5.0.2.17")])]});
            var Q71;
            Q71=makeQuery(id+"F1.opExtrude","SWEPT_EDGE",EDGE,{"disambiguationData":[OSD([sQuery(id+"F0.wireOp",EDGE,"E5.0.1.1"),sQuery(id+"F0.wireOp",EDGE,"E5.0.1.17")])]});
            var Q72;
            Q72=makeQuery(id+"F1.opExtrude","SWEPT_EDGE",EDGE,{"disambiguationData":[OSD([sQuery(id+"F0.wireOp",EDGE,"E2.2.0.1"),sQuery(id+"F0.wireOp",EDGE,"E2.2.0.2")])]});
            var Q73;
            Q73=makeQuery(id+"F1.opExtrude","SWEPT_EDGE",EDGE,{"disambiguationData":[OSD([sQuery(id+"F0.wireOp",EDGE,"E3.3.2.1"),sQuery(id+"F0.wireOp",EDGE,"E3.6.2.1")])]});
            var Q74;
            Q74=makeQuery(id+"F1.opExtrude","SWEPT_EDGE",EDGE,{"disambiguationData":[OSD([sQuery(id+"F0.wireOp",EDGE,"E3.3.2.2"),sQuery(id+"F0.wireOp",EDGE,"E3.6.2.2")])]});
            var Q75;
            Q75=makeQuery(id+"F1.opExtrude","SWEPT_EDGE",EDGE,{"disambiguationData":[OSD([sQuery(id+"F0.wireOp",EDGE,"E4.2.0.4"),sQuery(id+"F0.wireOp",EDGE,"E4.2.0.5")])]});
            var Q76;
            Q76=makeQuery(id+"F1.opExtrude","SWEPT_EDGE",EDGE,{"disambiguationData":[OSD([sQuery(id+"F0.wireOp",EDGE,"E4.2.0.2"),sQuery(id+"F0.wireOp",EDGE,"E4.2.0.7")])]});
            var Q77;
            Q77=makeQuery(id+"F1.opExtrude","SWEPT_EDGE",EDGE,{"disambiguationData":[OSD([sQuery(id+"F0.wireOp",EDGE,"E5.0.1.8"),sQuery(id+"F0.wireOp",EDGE,"E5.0.1.15")])]});
            var Q78;
            Q78=makeQuery(id+"F1.opExtrude","SWEPT_EDGE",EDGE,{"disambiguationData":[OSD([sQuery(id+"F0.wireOp",EDGE,"E5.0.2.8"),sQuery(id+"F0.wireOp",EDGE,"E5.0.2.15")])]});
            var Q79;
            Q79=makeQuery(id+"F1.opExtrude","SWEPT_EDGE",EDGE,{"disambiguationData":[OSD([sQuery(id+"F0.wireOp",EDGE,"E5.0.2.2"),sQuery(id+"F0.wireOp",EDGE,"E5.0.2.4")])]});
            var Q80;
            Q80=makeQuery(id+"F1.opExtrude","SWEPT_EDGE",EDGE,{"disambiguationData":[OSD([sQuery(id+"F0.wireOp",EDGE,"E5.0.1.2"),sQuery(id+"F0.wireOp",EDGE,"E5.0.1.4")])]});
            var Q81;
            Q81=makeQuery(id+"F1.opExtrude","SWEPT_EDGE",EDGE,{"disambiguationData":[OSD([sQuery(id+"F0.wireOp",EDGE,"E4.1.0.2"),sQuery(id+"F0.wireOp",EDGE,"E4.1.0.7")])]});
            var Q82;
            Q82=makeQuery(id+"F1.opExtrude","SWEPT_EDGE",EDGE,{"disambiguationData":[OSD([sQuery(id+"F0.wireOp",EDGE,"E4.1.0.3"),sQuery(id+"F0.wireOp",EDGE,"E4.1.0.12")])]});
            var Q83;
            Q83=makeQuery(id+"F1.opExtrude","SWEPT_EDGE",EDGE,{"disambiguationData":[OSD([sQuery(id+"F0.wireOp",EDGE,"E4.1.0.4"),sQuery(id+"F0.wireOp",EDGE,"E4.1.0.5")])]});
            var Q84;
            Q84=makeQuery(id+"F1.opExtrude","SWEPT_EDGE",EDGE,{"disambiguationData":[OSD([sQuery(id+"F0.wireOp",EDGE,"E3.0.0.2"),sQuery(id+"F0.wireOp",EDGE,"E3.9.0.2")])]});
            var Q85;
            Q85=makeQuery(id+"F1.opExtrude","SWEPT_EDGE",EDGE,{"disambiguationData":[OSD([sQuery(id+"F0.wireOp",EDGE,"E3.0.0.1"),sQuery(id+"F0.wireOp",EDGE,"E3.9.0.1")])]});
            var Q86;
            Q86=makeQuery(id+"F1.opExtrude","SWEPT_EDGE",EDGE,{"disambiguationData":[OSD([sQuery(id+"F0.wireOp",EDGE,"E1.bottom"),sQuery(id+"F0.wireOp",EDGE,"E1.left")])]});
            var Q87;
            Q87=makeQuery(id+"F1.opExtrude","SWEPT_EDGE",EDGE,{"disambiguationData":[OSD([sQuery(id+"F0.wireOp",EDGE,"E4.2.0.3"),sQuery(id+"F0.wireOp",EDGE,"E4.2.0.12")])]});
            var Q88;
            Q88=makeQuery(id+"F1.opExtrude","SWEPT_EDGE",EDGE,{"disambiguationData":[OSD([sQuery(id+"F0.wireOp",EDGE,"E5.0.1.7"),sQuery(id+"F0.wireOp",EDGE,"E5.0.1.25")])]});
            var Q89;
            Q89=makeQuery(id+"F1.opExtrude","SWEPT_EDGE",EDGE,{"disambiguationData":[OSD([sQuery(id+"F0.wireOp",EDGE,"E5.0.2.7"),sQuery(id+"F0.wireOp",EDGE,"E5.0.2.25")])]});
            var Q90;
            Q90=makeQuery(id+"F1.opExtrude","SWEPT_EDGE",EDGE,{"disambiguationData":[OSD([sQuery(id+"F0.wireOp",EDGE,"E5.0.2.5"),sQuery(id+"F0.wireOp",EDGE,"E5.0.2.13")])]});
            var Q91;
            Q91=makeQuery(id+"F1.opExtrude","SWEPT_EDGE",EDGE,{"disambiguationData":[OSD([sQuery(id+"F0.wireOp",EDGE,"E5.0.1.5"),sQuery(id+"F0.wireOp",EDGE,"E5.0.1.13")])]});
            var Q92;
            Q92=makeQuery(id+"F1.opExtrude","SWEPT_EDGE",EDGE,{"disambiguationData":[OSD([sQuery(id+"F0.wireOp",EDGE,"E2.1.0.0"),sQuery(id+"F0.wireOp",EDGE,"E2.1.0.3")])]});
            var Q93;
            Q93=makeQuery(id+"F1.opExtrude","SWEPT_EDGE",EDGE,{"disambiguationData":[OSD([sQuery(id+"F0.wireOp",EDGE,"E3.0.1.1"),sQuery(id+"F0.wireOp",EDGE,"E3.9.1.1")])]});
            var Q94;
            Q94=makeQuery(id+"F1.opExtrude","SWEPT_EDGE",EDGE,{"disambiguationData":[OSD([sQuery(id+"F0.wireOp",EDGE,"E3.0.2.2"),sQuery(id+"F0.wireOp",EDGE,"E3.9.2.2")])]});
            var Q95;
            Q95=makeQuery(id+"F1.opExtrude","SWEPT_EDGE",EDGE,{"disambiguationData":[OSD([sQuery(id+"F0.wireOp",EDGE,"E5.0.1.14"),sQuery(id+"F0.wireOp",EDGE,"E5.0.1.21")])]});
            var Q96;
            Q96=makeQuery(id+"F1.opExtrude","SWEPT_EDGE",EDGE,{"disambiguationData":[OSD([sQuery(id+"F0.wireOp",EDGE,"E5.0.2.14"),sQuery(id+"F0.wireOp",EDGE,"E5.0.2.21")])]});
            var Q97;
            Q97=makeQuery(id+"F1.opExtrude","SWEPT_EDGE",EDGE,{"disambiguationData":[OSD([sQuery(id+"F0.wireOp",EDGE,"E2.2.0.0"),sQuery(id+"F0.wireOp",EDGE,"E2.2.0.3")])]});
            var Q98;
            Q98=makeQuery(id+"F1.opExtrude","SWEPT_EDGE",EDGE,{"disambiguationData":[OSD([sQuery(id+"F0.wireOp",EDGE,"E3.0.2.1"),sQuery(id+"F0.wireOp",EDGE,"E3.9.2.1")])]});
            var Q99;
            Q99=makeQuery(id+"F1.opExtrude","SWEPT_EDGE",EDGE,{"disambiguationData":[OSD([sQuery(id+"F0.wireOp",EDGE,"E3.0.1.2"),sQuery(id+"F0.wireOp",EDGE,"E3.9.1.2")])]});
            fillet(context, id + "F3", {"entities" : qUnion([Q0, Q1, Q2, Q3, Q4, Q5, Q6, Q7, Q8, Q9, Q10, Q11, Q12, Q13, Q14, Q15, Q16, Q17, Q18, Q19, Q20, Q21, Q22, Q23, Q24, Q25, Q26, Q27, Q28, Q29, Q30, Q31, Q32, Q33, Q34, Q35, Q36, Q37, Q38, Q39, Q40, Q41, Q42, Q43, Q44, Q45, Q46, Q47, Q48, Q49, Q50, Q51, Q52, Q53, Q54, Q55, Q56, Q57, Q58, Q59, Q60, Q61, Q62, Q63, Q64, Q65, Q66, Q67, Q68, Q69, Q70, Q71, Q72, Q73, Q74, Q75, Q76, Q77, Q78, Q79, Q80, Q81, Q82, Q83, Q84, Q85, Q86, Q87, Q88, Q89, Q90, Q91, Q92, Q93, Q94, Q95, Q96, Q97, Q98, Q99]), "radius" : 0.64 * mm, "tangentPropagation" : true, "allowEdgeOverflow" : false});
        }
        {
            var Q0;
            Q0=makeQuery(id+"F1.opExtrude","SWEPT_EDGE",EDGE,{"disambiguationData":[OSD([sQuery(id+"F0.wireOp",EDGE,"E0.bottom"),sQuery(id+"F0.wireOp",EDGE,"E0.right")])]});
            var Q1;
            Q1=makeQuery(id+"F1.opExtrude","SWEPT_EDGE",EDGE,{"disambiguationData":[OSD([sQuery(id+"F0.wireOp",EDGE,"E0.bottom"),sQuery(id+"F0.wireOp",EDGE,"E0.left")])]});
            var Q2;
            Q2=makeQuery(id+"F1.opExtrude","SWEPT_EDGE",EDGE,{"disambiguationData":[OSD([sQuery(id+"F0.wireOp",EDGE,"E0.top"),sQuery(id+"F0.wireOp",EDGE,"E0.left")])]});
            var Q3;
            Q3=makeQuery(id+"F1.opExtrude","SWEPT_EDGE",EDGE,{"disambiguationData":[OSD([sQuery(id+"F0.wireOp",EDGE,"E0.top"),sQuery(id+"F0.wireOp",EDGE,"E0.right")])]});
            fillet(context, id + "F4", {"entities" : qUnion([Q0, Q1, Q2, Q3]), "radius" : 5.08 * mm, "tangentPropagation" : true, "allowEdgeOverflow" : false});
        }
        {
            var Q0;
            Q0=makeQuery(id+"F1.opExtrude","CAP_FACE",FACE,{"disambiguationData":[OSD([sQuery(id+"F0.wireOp",EDGE,"E0.bottom"),sQuery(id+"F0.wireOp",EDGE,"E0.top"),sQuery(id+"F0.wireOp",EDGE,"E0.left"),sQuery(id+"F0.wireOp",EDGE,"E0.right"),sQuery(id+"F0.wireOp",EDGE,"E1.bottom"),sQuery(id+"F0.wireOp",EDGE,"E1.top"),sQuery(id+"F0.wireOp",EDGE,"E1.left"),sQuery(id+"F0.wireOp",EDGE,"E1.right"),sQuery(id+"F0.wireOp",EDGE,"E2.1.0.0"),sQuery(id+"F0.wireOp",EDGE,"E2.1.0.1"),sQuery(id+"F0.wireOp",EDGE,"E2.1.0.2"),sQuery(id+"F0.wireOp",EDGE,"E2.1.0.3"),sQuery(id+"F0.wireOp",EDGE,"E2.2.0.0"),sQuery(id+"F0.wireOp",EDGE,"E2.2.0.1"),sQuery(id+"F0.wireOp",EDGE,"E2.2.0.2"),sQuery(id+"F0.wireOp",EDGE,"E2.2.0.3"),sQuery(id+"F0.wireOp",EDGE,"E3.0.0.1"),sQuery(id+"F0.wireOp",EDGE,"E3.3.0.1"),sQuery(id+"F0.wireOp",EDGE,"E3.6.0.1"),sQuery(id+"F0.wireOp",EDGE,"E3.9.0.1"),sQuery(id+"F0.wireOp",EDGE,"E3.0.0.2"),sQuery(id+"F0.wireOp",EDGE,"E3.3.0.2"),sQuery(id+"F0.wireOp",EDGE,"E3.6.0.2"),sQuery(id+"F0.wireOp",EDGE,"E3.9.0.2"),sQuery(id+"F0.wireOp",EDGE,"E3.0.1.1"),sQuery(id+"F0.wireOp",EDGE,"E3.3.1.1"),sQuery(id+"F0.wireOp",EDGE,"E3.6.1.1"),sQuery(id+"F0.wireOp",EDGE,"E3.9.1.1"),sQuery(id+"F0.wireOp",EDGE,"E3.0.1.2"),sQuery(id+"F0.wireOp",EDGE,"E3.3.1.2"),sQuery(id+"F0.wireOp",EDGE,"E3.6.1.2"),sQuery(id+"F0.wireOp",EDGE,"E3.9.1.2"),sQuery(id+"F0.wireOp",EDGE,"E3.0.2.1"),sQuery(id+"F0.wireOp",EDGE,"E3.3.2.1"),sQuery(id+"F0.wireOp",EDGE,"E3.6.2.1"),sQuery(id+"F0.wireOp",EDGE,"E3.9.2.1"),sQuery(id+"F0.wireOp",EDGE,"E3.0.2.2"),sQuery(id+"F0.wireOp",EDGE,"E3.3.2.2"),sQuery(id+"F0.wireOp",EDGE,"E3.6.2.2"),sQuery(id+"F0.wireOp",EDGE,"E3.9.2.2"),sQuery(id+"F0.wireOp",EDGE,"E4.1.0.1"),sQuery(id+"F0.wireOp",EDGE,"E4.1.0.2"),sQuery(id+"F0.wireOp",EDGE,"E4.1.0.3"),sQuery(id+"F0.wireOp",EDGE,"E4.1.0.4"),sQuery(id+"F0.wireOp",EDGE,"E4.1.0.5"),sQuery(id+"F0.wireOp",EDGE,"E4.1.0.6"),sQuery(id+"F0.wireOp",EDGE,"E4.1.0.7"),sQuery(id+"F0.wireOp",EDGE,"E4.1.0.9"),sQuery(id+"F0.wireOp",EDGE,"E4.1.0.10"),sQuery(id+"F0.wireOp",EDGE,"E4.1.0.11"),sQuery(id+"F0.wireOp",EDGE,"E4.1.0.12"),sQuery(id+"F0.wireOp",EDGE,"E4.1.0.14"),sQuery(id+"F0.wireOp",EDGE,"E4.2.0.1"),sQuery(id+"F0.wireOp",EDGE,"E4.2.0.2"),sQuery(id+"F0.wireOp",EDGE,"E4.2.0.3"),sQuery(id+"F0.wireOp",EDGE,"E4.2.0.4"),sQuery(id+"F0.wireOp",EDGE,"E4.2.0.5"),sQuery(id+"F0.wireOp",EDGE,"E4.2.0.6"),sQuery(id+"F0.wireOp",EDGE,"E4.2.0.7"),sQuery(id+"F0.wireOp",EDGE,"E4.2.0.9"),sQuery(id+"F0.wireOp",EDGE,"E4.2.0.10"),sQuery(id+"F0.wireOp",EDGE,"E4.2.0.11"),sQuery(id+"F0.wireOp",EDGE,"E4.2.0.12"),sQuery(id+"F0.wireOp",EDGE,"E4.2.0.14"),sQuery(id+"F0.wireOp",EDGE,"E5.0.1.1"),sQuery(id+"F0.wireOp",EDGE,"E5.0.1.2"),sQuery(id+"F0.wireOp",EDGE,"E5.0.1.3"),sQuery(id+"F0.wireOp",EDGE,"E5.0.1.4"),sQuery(id+"F0.wireOp",EDGE,"E5.0.1.5"),sQuery(id+"F0.wireOp",EDGE,"E5.0.1.7"),sQuery(id+"F0.wireOp",EDGE,"E5.0.1.8"),sQuery(id+"F0.wireOp",EDGE,"E5.0.1.9"),sQuery(id+"F0.wireOp",EDGE,"E5.0.1.11"),sQuery(id+"F0.wireOp",EDGE,"E5.0.1.12"),sQuery(id+"F0.wireOp",EDGE,"E5.0.1.13"),sQuery(id+"F0.wireOp",EDGE,"E5.0.1.14"),sQuery(id+"F0.wireOp",EDGE,"E5.0.1.15"),sQuery(id+"F0.wireOp",EDGE,"E5.0.1.16"),sQuery(id+"F0.wireOp",EDGE,"E5.0.1.17"),sQuery(id+"F0.wireOp",EDGE,"E5.0.1.19"),sQuery(id+"F0.wireOp",EDGE,"E5.0.1.20"),sQuery(id+"F0.wireOp",EDGE,"E5.0.1.21"),sQuery(id+"F0.wireOp",EDGE,"E5.0.1.22"),sQuery(id+"F0.wireOp",EDGE,"E5.0.1.25"),sQuery(id+"F0.wireOp",EDGE,"E5.0.2.1"),sQuery(id+"F0.wireOp",EDGE,"E5.0.2.2"),sQuery(id+"F0.wireOp",EDGE,"E5.0.2.3"),sQuery(id+"F0.wireOp",EDGE,"E5.0.2.4"),sQuery(id+"F0.wireOp",EDGE,"E5.0.2.5"),sQuery(id+"F0.wireOp",EDGE,"E5.0.2.7"),sQuery(id+"F0.wireOp",EDGE,"E5.0.2.8"),sQuery(id+"F0.wireOp",EDGE,"E5.0.2.9"),sQuery(id+"F0.wireOp",EDGE,"E5.0.2.11"),sQuery(id+"F0.wireOp",EDGE,"E5.0.2.12"),sQuery(id+"F0.wireOp",EDGE,"E5.0.2.13"),sQuery(id+"F0.wireOp",EDGE,"E5.0.2.14"),sQuery(id+"F0.wireOp",EDGE,"E5.0.2.15"),sQuery(id+"F0.wireOp",EDGE,"E5.0.2.16"),sQuery(id+"F0.wireOp",EDGE,"E5.0.2.17"),sQuery(id+"F0.wireOp",EDGE,"E5.0.2.19"),sQuery(id+"F0.wireOp",EDGE,"E5.0.2.20"),sQuery(id+"F0.wireOp",EDGE,"E5.0.2.21"),sQuery(id+"F0.wireOp",EDGE,"E5.0.2.22"),sQuery(id+"F0.wireOp",EDGE,"E5.0.2.25")])],"isStart":false});
            var Q1;
            Q1=makeQuery(id+"F1.opExtrude","CAP_EDGE",EDGE,{"disambiguationData":[OSD([sQuery(id+"F0.wireOp",EDGE,"E0.top")])],"isStart":true});
            chamfer(context, id + "F5", {"entities" : qUnion([Q0, Q1]), "width" : 1.59 * mm, "tangentPropagation" : true});
        }
    });
